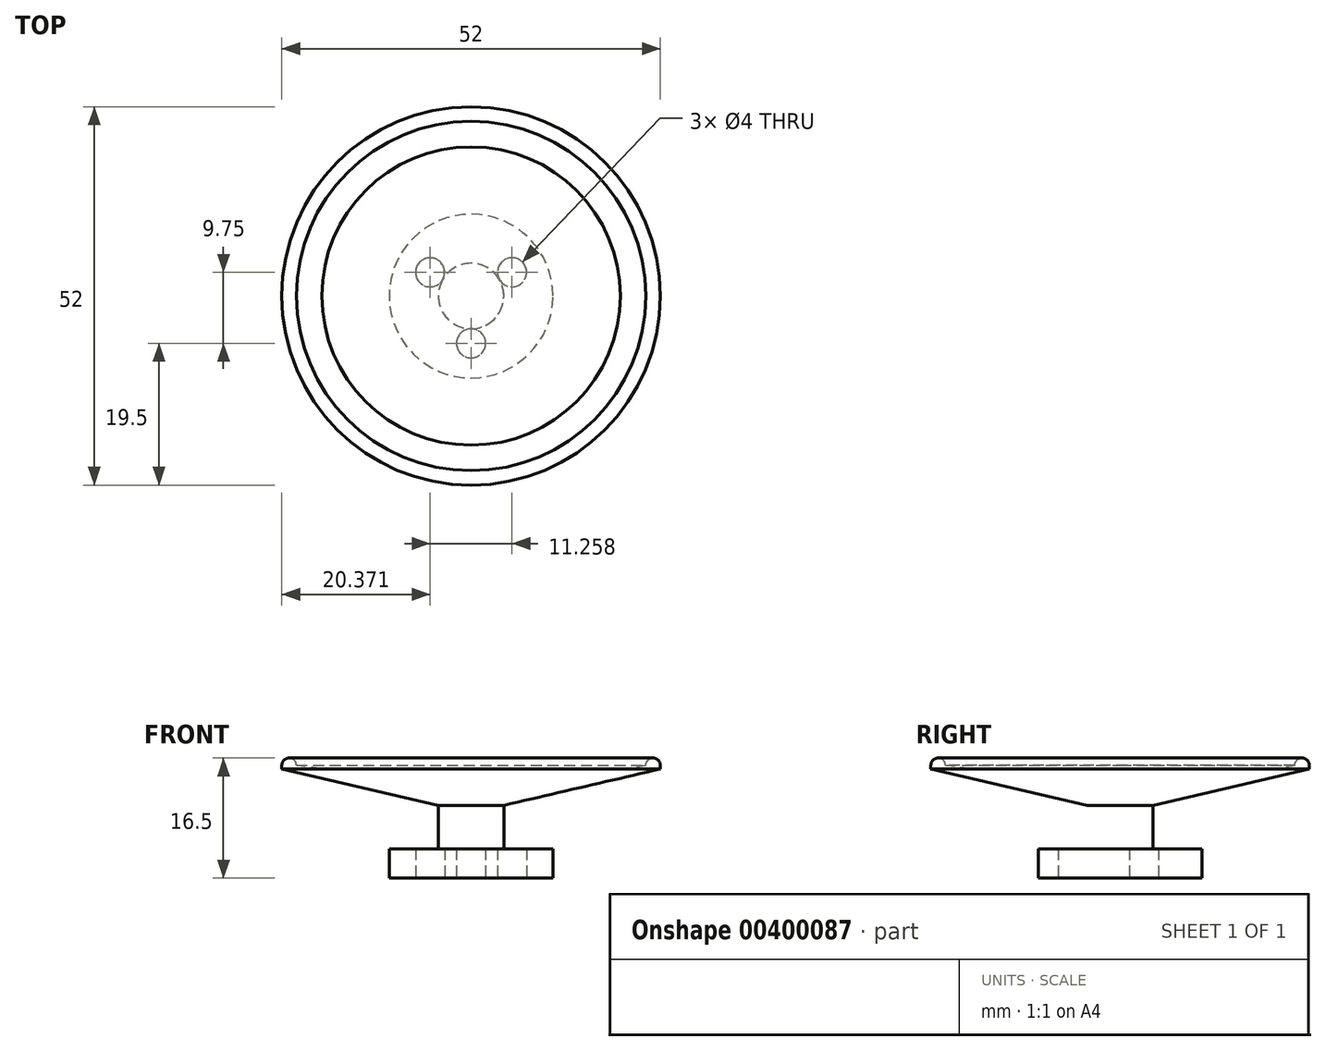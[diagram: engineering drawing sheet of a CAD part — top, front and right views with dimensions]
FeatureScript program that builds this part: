
annotation { "Feature Type Name" : "Feature", "Feature Type Description" : "" }
export const myFeature = defineFeature(function(context is Context, id is Id, definition is map)
    precondition{}
    {
        {
            var Q0;
            Q0=qCreatedBy(makeId("Top.planeOp"),FACE);
            var sketch = newSketch(context, id + "F0", { "sketchPlane" : qUnion([Q0])});
            skCircle(sketch, "E0", {"center": v(0, 0) * mm, "radius": 11.25 * mm});
            skSolve(sketch);
        }
        {
            var Q0;
            Q0=qSketchRegion(id+"F0",true);
            extrude(context, id + "F1", {"entities" : qUnion([Q0]), "depth" : 4 * mm});
        }
        {
            var Q0;
            Q0=makeQuery(id+"F1.opExtrude","CAP_FACE",FACE,{"disambiguationData":[OSD([sQuery(id+"F0.wireOp",EDGE,"E0")])],"isStart":false});
            var sketch = newSketch(context, id + "F2", { "sketchPlane" : qUnion([Q0])});
            skCircle(sketch, "E1", {"center": v(0, 0) * mm, "radius": 4.5 * mm});
            skSolve(sketch);
        }
        {
            var Q0;
            Q0=qSketchRegion(id+"F2",true);
            extrude(context, id + "F3", {"entities" : qUnion([Q0]), "operationType" : NewBodyOperationType.ADD, "depth" : 6 * mm});
        }
        {
            var Q0;
            Q0=qCreatedBy(makeId("Front.planeOp"),FACE);
            var sketch = newSketch(context, id + "F4", { "sketchPlane" : qUnion([Q0])});
            skLineSegment(sketch, "E2", {"start": v(0, 15) * mm, "end": v(20.5, 15) * mm});
            skLineSegment(sketch, "E3", {"start": v(20.5, 15) * mm, "end": v(24, 15.5) * mm});
            skLineSegment(sketch, "E4.0", {"start": v(0, 10) * mm, "end": v(4.5, 10) * mm});
            skLineSegment(sketch, "E5", {"start": v(0, 0) * mm, "end": v(0, 38.4) * mm, "construction": true});
            skLineSegment(sketch, "E6", {"start": v(24, 15.5) * mm, "end": v(26, 15.5) * mm, "construction": true});
            skArc(sketch, "E7", {"start": v(26, 15.5) * mm, "mid": v(25, 16.5) * mm, "end": v(24, 15.5) * mm});
            skLineSegment(sketch, "E8", {"start": v(20.84, 16.5) * mm, "end": v(29.48, 16.5) * mm, "construction": true});
            skLineSegment(sketch, "E9", {"start": v(0, 15) * mm, "end": v(0, 10) * mm});
            skLineSegment(sketch, "E10", {"start": v(4.5, 10) * mm, "end": v(26, 15) * mm});
            skLineSegment(sketch, "E11", {"start": v(26, 15) * mm, "end": v(26, 15.5) * mm});
            skSolve(sketch);
        }
        {
            var Q0;
            Q0=qSketchRegion(id+"F4",true);
            var Q1;
            Q1=sQuery(id+"F4.wireOp",EDGE,"E5");
            revolve(context, id + "F5", {"operationType" : NewBodyOperationType.ADD, "entities" : qUnion([Q0]), "axis" : qUnion([Q1]), "revolveType" : RevolveType.FULL});
        }
        {
            var Q0;
            Q0=makeQuery(id+"F1.opExtrude","CAP_FACE",FACE,{"disambiguationData":[OSD([sQuery(id+"F0.wireOp",EDGE,"E0")])],"isStart":true});
            var sketch = newSketch(context, id + "F6", { "sketchPlane" : qUnion([Q0])});
            skCircle(sketch, "E12", {"center": v(0, 6.5) * mm, "radius": 2 * mm});
            skCircle(sketch, "E13.1.0", {"center": v(-5.63, -3.25) * mm, "radius": 2 * mm});
            skCircle(sketch, "E13.2.0", {"center": v(5.63, -3.25) * mm, "radius": 2 * mm});
            skPoint(sketch, "E13.center", {"position": v(0, 0) * mm});
            skSolve(sketch);
        }
        {
            var Q0;
            Q0=makeQuery(id+"F6.imprint","IMPRINT",FACE,{"disambiguationData":[TD([[makeQuery(id+"F6.imprint","IMPRINT",EDGE,{"derivedFrom":sQuery(id+"F6.wireOp",EDGE,"E13.1.0")}),1.0]])]});
            var Q1;
            Q1=makeQuery(id+"F6.imprint","IMPRINT",FACE,{"disambiguationData":[TD([[makeQuery(id+"F6.imprint","IMPRINT",EDGE,{"derivedFrom":sQuery(id+"F6.wireOp",EDGE,"E13.2.0")}),1.0]])]});
            var Q2;
            Q2=makeQuery(id+"F6.imprint","IMPRINT",FACE,{"disambiguationData":[TD([[makeQuery(id+"F6.imprint","IMPRINT",EDGE,{"derivedFrom":sQuery(id+"F6.wireOp",EDGE,"E12")}),1.0]])]});
            var Q3;
            Q3=makeQuery(id+"F1.opExtrude","CAP_FACE",FACE,{"disambiguationData":[OSD([sQuery(id+"F0.wireOp",EDGE,"E0")])],"isStart":false});
            extrude(context, id + "F7", {"entities" : qUnion([Q0, Q1, Q2]), "operationType" : NewBodyOperationType.REMOVE, "endBound" : BoundingType.UP_TO_SURFACE, "oppositeDirection" : true, "endBoundEntityFace" : qUnion([Q3]), "depth" : 25 * mm});
        }
    });
